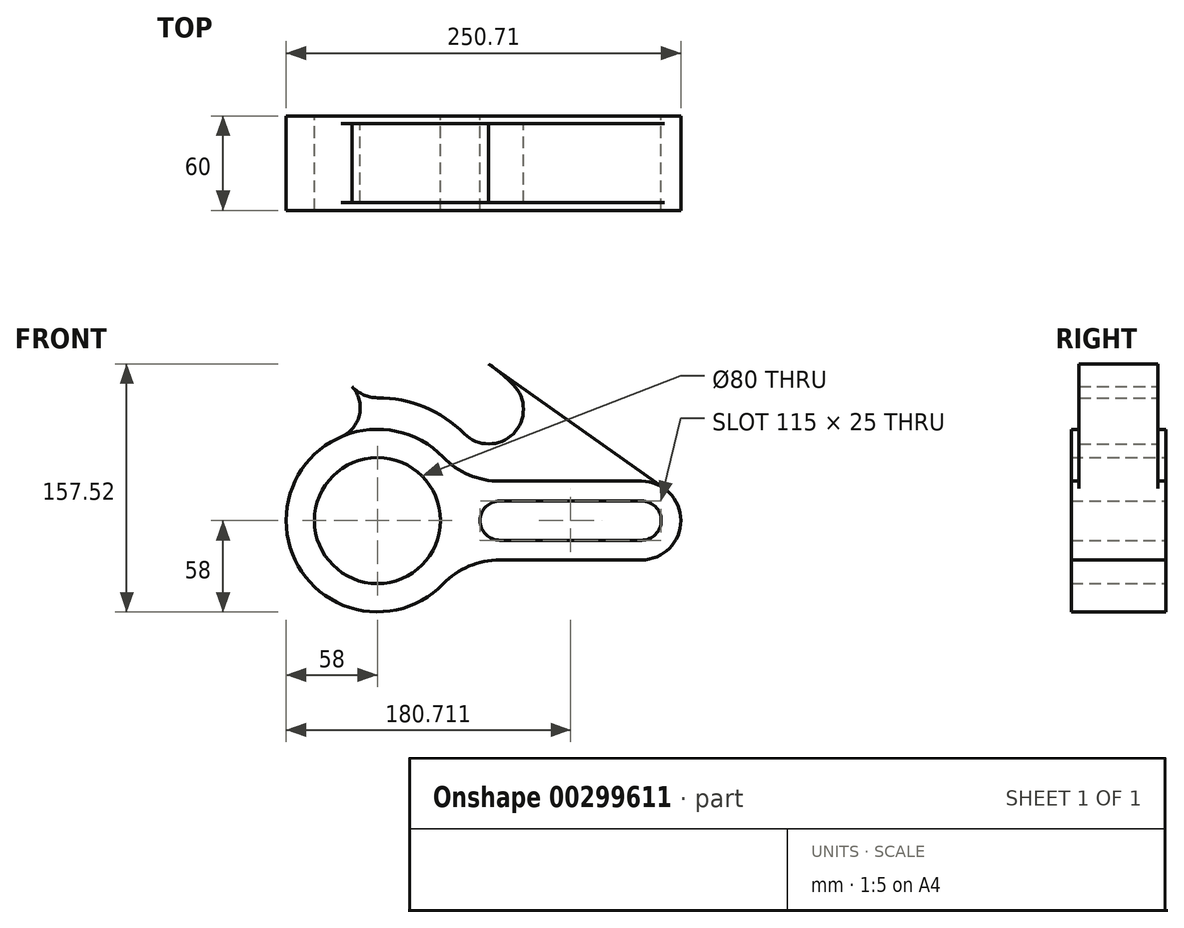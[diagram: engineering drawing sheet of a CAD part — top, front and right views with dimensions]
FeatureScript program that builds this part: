
annotation { "Feature Type Name" : "Feature", "Feature Type Description" : "" }
export const myFeature = defineFeature(function(context is Context, id is Id, definition is map)
    precondition{}
    {
        {
            var Q0;
            Q0=qCreatedBy(makeId("Front.planeOp"),FACE);
            var sketch = newSketch(context, id + "F0", { "sketchPlane" : qUnion([Q0])});
            skArc(sketch, "E0", {"start": v(77.71, -25) * mm, "mid": v(58.17, -28.98) * mm, "end": v(41.73, -40.28) * mm});
            skLineSegment(sketch, "E1", {"start": v(77.71, 25) * mm, "end": v(167.71, 25) * mm});
            skArc(sketch, "E2", {"start": v(77.71, 12.5) * mm, "mid": v(65.21, 0) * mm, "end": v(77.71, -12.5) * mm});
            skArc(sketch, "E3", {"start": v(167.71, -12.5) * mm, "mid": v(180.21, 0) * mm, "end": v(167.71, 12.5) * mm});
            skLineSegment(sketch, "E4", {"start": v(77.71, 12.5) * mm, "end": v(167.71, 12.5) * mm});
            skLineSegment(sketch, "E5", {"start": v(77.71, -12.5) * mm, "end": v(167.71, -12.5) * mm});
            skLineSegment(sketch, "E6", {"start": v(77.71, -25) * mm, "end": v(167.71, -25) * mm});
            skArc(sketch, "E7", {"start": v(41.73, 40.28) * mm, "mid": v(58.17, 28.98) * mm, "end": v(77.71, 25) * mm});
            skArc(sketch, "E8", {"start": v(167.71, -25) * mm, "mid": v(192.71, 0) * mm, "end": v(167.71, 25) * mm});
            skArc(sketch, "E9", {"start": v(41.73, 40.28) * mm, "mid": v(-58, 0) * mm, "end": v(41.73, -40.28) * mm});
            skCircle(sketch, "E10", {"center": v(0, 0) * mm, "radius": 40 * mm});
            skLineSegment(sketch, "E11", {"start": v(0, 0) * mm, "end": v(0, 122) * mm, "construction": true});
            skLineSegment(sketch, "E12", {"start": v(0, 0) * mm, "end": v(111.29, 111.29) * mm, "construction": true});
            skArc(sketch, "E13", {"start": v(-26.35, 96.47) * mm, "mid": v(36.15, 93.24) * mm, "end": v(84.49, 53.5) * mm, "construction": true});
            skArc(sketch, "E14", {"start": v(86.27, 86.27) * mm, "mid": v(46.69, 112.71) * mm, "end": v(0, 122) * mm});
            skLineSegment(sketch, "E15", {"start": v(70.56, 99.52) * mm, "end": v(182.17, 20.4) * mm});
            skPoint(sketch, "E15.startSnap0", {"position": v(70.56, 85.52) * mm});
            skArc(sketch, "E16", {"start": v(0, 122) * mm, "mid": v(-22, 100) * mm, "end": v(0, 78) * mm});
            skArc(sketch, "E17", {"start": v(86.27, 86.27) * mm, "mid": v(86.27, 55.15) * mm, "end": v(55.15, 55.15) * mm});
            skArc(sketch, "E18", {"start": v(0, 78) * mm, "mid": v(29.85, 72.06) * mm, "end": v(55.15, 55.15) * mm});
            skArc(sketch, "E19", {"start": v(0, 109) * mm, "mid": v(-9, 100) * mm, "end": v(0, 91) * mm});
            skArc(sketch, "E20", {"start": v(-23, 53.24) * mm, "mid": v(-11.38, 67.43) * mm, "end": v(-16.2, 85.12) * mm});
            skArc(sketch, "E21", {"start": v(0, 109) * mm, "mid": v(41.71, 100.7) * mm, "end": v(77.07, 77.07) * mm});
            skArc(sketch, "E22", {"start": v(0, 91) * mm, "mid": v(34.82, 84.07) * mm, "end": v(64.35, 64.35) * mm});
            skArc(sketch, "E23", {"start": v(77.07, 77.07) * mm, "mid": v(77.07, 64.35) * mm, "end": v(64.35, 64.35) * mm});
            skSolve(sketch);
        }
        {
            var Q0;
            {var subQ5=sQuery(id+"F0.wireOp",EDGE,"E0");Q0=makeQuery(id+"F0.imprint","IMPRINT",FACE,{"disambiguationData":[TD([[makeQuery(id+"F0.imprint","IMPRINT",EDGE,{"derivedFrom":subQ5}),-1.0]])]});}
            extrude(context, id + "F1", {"entities" : qUnion([Q0]), "endBound" : BoundingType.SYMMETRIC, "depth" : 60 * mm});
        }
        {
            var Q0;
            {var subQ4=sQuery(id+"F0.wireOp",EDGE,"E1");Q0=makeQuery(id+"F0.imprint","IMPRINT",FACE,{"disambiguationData":[TD([[makeQuery(id+"F0.imprint","IMPRINT",EDGE,{"derivedFrom":subQ4}),1.0]])]});}
            extrude(context, id + "F2", {"entities" : qUnion([Q0]), "operationType" : NewBodyOperationType.ADD, "endBound" : BoundingType.SYMMETRIC, "depth" : 30 * mm});
        }
        {
            var Q0;
            {var subQ6=sQuery(id+"F0.wireOp",EDGE,"E17");Q0=makeQuery(id+"F0.imprint","IMPRINT",FACE,{"disambiguationData":[TD([[makeQuery(id+"F0.imprint","IMPRINT",EDGE,{"derivedFrom":subQ6}),-1.0]])]});}
            extrude(context, id + "F3", {"entities" : qUnion([Q0]), "operationType" : NewBodyOperationType.ADD, "endBound" : BoundingType.SYMMETRIC, "depth" : 50 * mm});
        }
    });
